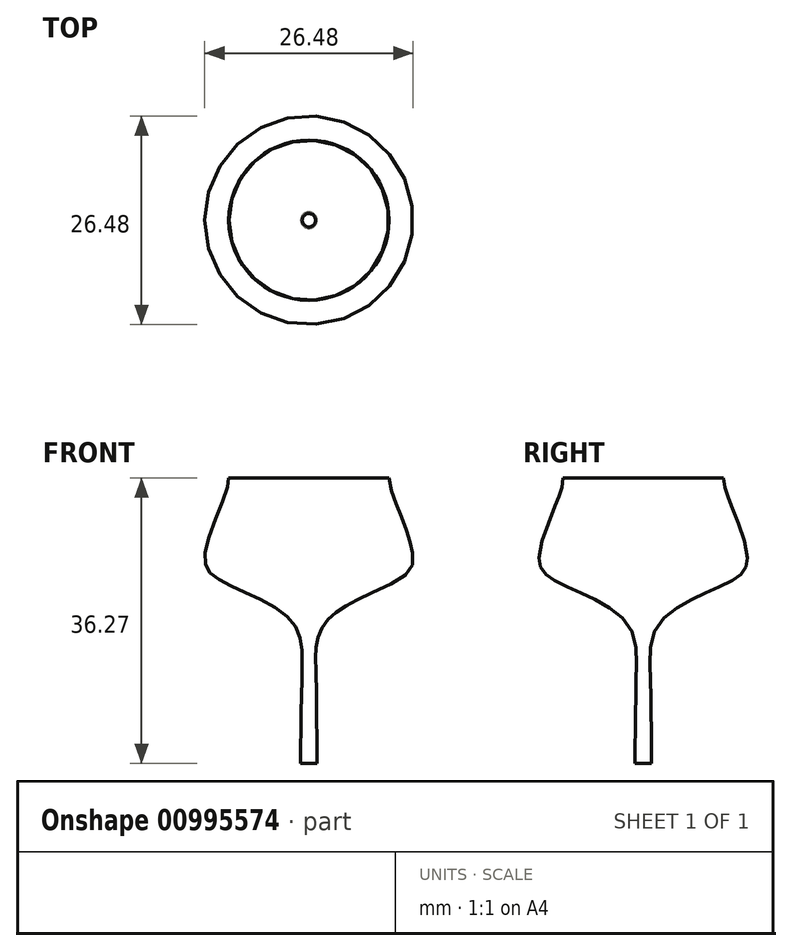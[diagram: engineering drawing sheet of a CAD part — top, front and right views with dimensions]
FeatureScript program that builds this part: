
annotation { "Feature Type Name" : "Feature", "Feature Type Description" : "" }
export const myFeature = defineFeature(function(context is Context, id is Id, definition is map)
    precondition{}
    {
        {
            var Q0;
            Q0=qCreatedBy(makeId("Front.planeOp"),FACE);
            var sketch = newSketch(context, id + "F0", { "sketchPlane" : qUnion([Q0])});
            skFitSpline(sketch, "E0", {"points": [v(-10.18, 48.5) * mm, v(-13.2, 38.9) * mm, v(-10.93, 35.31) * mm, v(-2.3, 30.42) * mm, v(-0.88, 23.73) * mm, v(-1.03, 12.24) * mm], "startDerivative": vector(4.07, -16.7) * mm, "endDerivative": vector(0.26, -47.34) * mm});
            skSolve(sketch);
        }
        {
            var Q0;
            Q0=qCreatedBy(makeId("Front.planeOp"),FACE);
            var sketch = newSketch(context, id + "F1", { "sketchPlane" : qUnion([Q0])});
            skLineSegment(sketch, "E1", {"start": v(0, 48.8) * mm, "end": v(0, 9.85) * mm});
            skSolve(sketch);
        }
        {
            var Q0;
            Q0 = qSketchRegion(id + "F0", true);
            var Q1;
            Q1 = qBodyType(qCreatedBy(id + "F0" ,EDGE), BodyType.WIRE);
            var Q2;
            Q2=sQuery(id+"F1.wireOp",EDGE,"E1");
            revolve(context, id + "F2", {"bodyType" : ToolBodyType.SURFACE, "surfaceOperationType" : NewSurfaceOperationType.NEW, "entities" : qUnion([Q0]), "surfaceEntities" : qUnion([Q1]), "axis" : qUnion([Q2]), "revolveType" : RevolveType.FULL});
        }
    });
